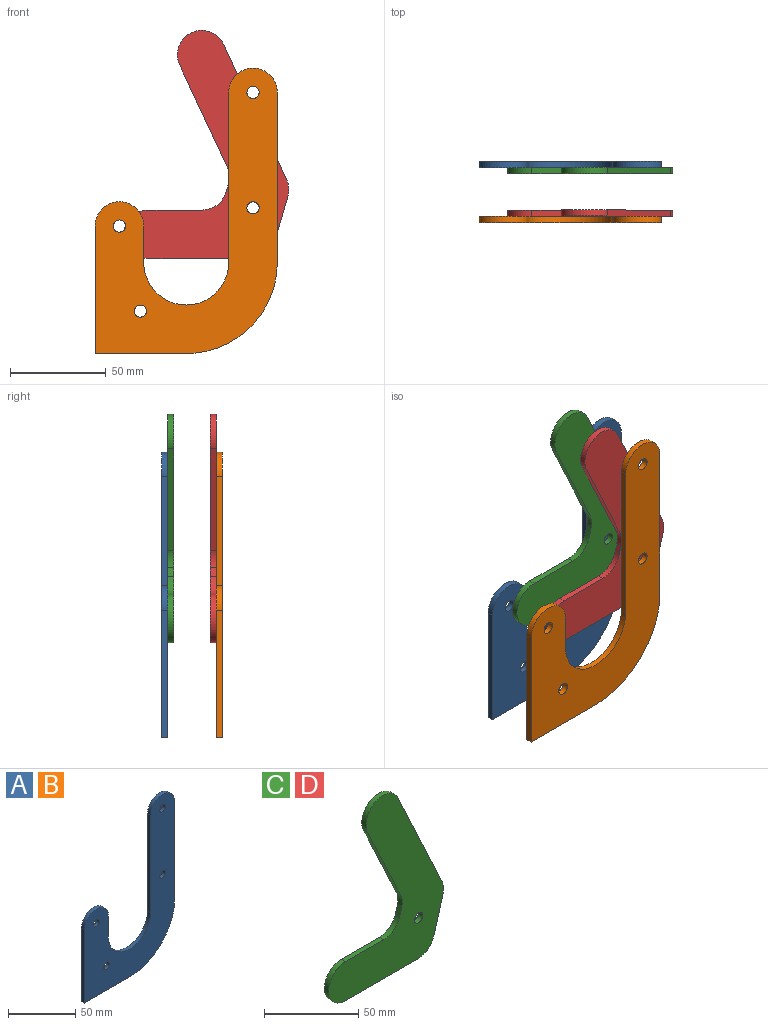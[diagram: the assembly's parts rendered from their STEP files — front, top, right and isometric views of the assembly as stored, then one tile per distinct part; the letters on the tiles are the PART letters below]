
ASSEMBLY  parts=4 mates=3
PART A: 15 faces, bbox 95.3x3.2x149.2 mm
  f0: plane 88.9x3.18mm, normal (-1,0,0), area 282.3mm2, adj f1,f8,f9,f10
  f1: cylinder r=22.23mm len=44.45mm, axis (0,1,0), area 221.7mm2, adj f0,f2,f9,f10
  f2: plane 19.05x3.18mm, normal (1,0,0), area 60.5mm2, adj f1,f3,f9,f10
  f3: cylinder r=12.7mm len=25.4mm, axis (0,1,0), area 126.7mm2, adj f2,f4,f9,f10
  f4: plane 66.68x3.18mm, normal (-1,0,0), area 211.7mm2, adj f3,f5,f9,f10
  f5: plane 47.63x3.18mm, normal (0,0,-1), area 151.2mm2, adj f4,f6,f9,f10
  f6: cylinder r=47.62mm len=47.63mm, axis (0,1,0), area 237.5mm2, adj f5,f7,f9,f10
  f7: plane 88.9x3.18mm, normal (1,0,0), area 282.3mm2, adj f6,f8,f9,f10
  f8: cylinder r=12.7mm len=25.4mm, axis (0,1,0), area 126.7mm2, adj f0,f7,f9,f10
  f9: plane 149.23x95.25mm, normal (0,-1,0), area 6395.6mm2, adj f0,f1,f2,f3,f4,f5,f6,f7
  f10: plane 149.23x95.25mm, normal (0,1,0), area 6395.6mm2, adj f0,f1,f2,f3,f4,f5,f6,f7
  f11: cylinder r=3.17mm len=6.35mm, axis (0,-1,0), area 63.3mm2, adj f9,f10
  f12: cylinder r=3.17mm len=6.35mm, axis (0,-1,0), area 63.3mm2, adj f9,f10
  f13: cylinder r=3.17mm len=6.35mm, axis (0,-1,0), area 63.3mm2, adj f9,f10
  f14: cylinder r=3.17mm len=6.35mm, axis (0,-1,0), area 63.3mm2, adj f9,f10
PART B: same geometry as A
PART C: 16 faces, bbox 86.4x3.2x119.3 mm
  f0: plane 28.56x3.18mm, normal (0,0,1), area 90.7mm2, adj f1,f2,f10,f15
  f1: plane 119.31x86.41mm, normal (0,-1,0), area 4540.3mm2, adj f0,f3,f4,f5,f6,f7,f8,f9
  f2: plane 119.31x86.41mm, normal (0,1,0), area 4540.3mm2, adj f0,f3,f4,f5,f6,f7,f8,f9
  f3: cylinder r=12.7mm len=8.91mm, axis (0,1,0), area 29mm2, adj f1,f2,f4,f14
  f4: plane 70.61x32.93mm, normal (0.91,0,0.42), area 247.4mm2, adj f1,f2,f3,f5
  f5: cylinder r=12.7mm len=24.21mm, axis (0,1,0), area 126.7mm2, adj f1,f2,f4,f6
  f6: plane 53.23x24.82mm, normal (-0.91,0,-0.42), area 186.5mm2, adj f1,f2,f5,f7
  f7: cylinder r=12.7mm len=8.91mm, axis (0,1,0), area 29mm2, adj f1,f2,f6,f8
  f8: plane 4.55x3.18mm, normal (-0.96,0,0.28), area 15.1mm2, adj f1,f2,f7,f9
  f9: plane 3.18x0.01mm, normal (-0.96,0,0.28), area 0mm2, adj f1,f2,f8,f10
  f10: cylinder r=12.7mm len=12.19mm, axis (0,1,0), area 51.9mm2, adj f0,f1,f2,f9
  f11: plane 54.25x3.18mm, normal (0,0,-1), area 172.2mm2, adj f1,f2,f12,f15
  f12: cylinder r=12.7mm len=12.2mm, axis (0,1,0), area 51.9mm2, adj f1,f2,f11,f14
  f13: cylinder r=3.17mm len=6.35mm, axis (0,1,0), area 63.3mm2, adj f1,f2
  f14: plane 23.3x6.76mm, normal (0.96,0,-0.28), area 77mm2, adj f1,f2,f3,f12
  f15: cylinder r=12.7mm len=25.4mm, axis (0,-1,0), area 126.7mm2, adj f0,f1,f2,f11
PART D: same geometry as C
PLACE A t=(43.05,40.82,-37)mm
PLACE B t=(43.05,12.24,-37)mm
PLACE C t=(52.53,37.64,12.01)mm
PLACE D t=(52.53,15.42,12.01)mm
MATE revolute D.f13 <-> B.f11  axis (0,-1,0) through (55.75,12.24,-8.43)mm
MATE revolute A.f11 <-> C.f13  axis (0,-1,0) through (55.75,37.64,-8.43)mm
MATE fastened B.f11 <-> A.f11  axis (0,1,0) through (55.75,12.24,-8.43)mm
